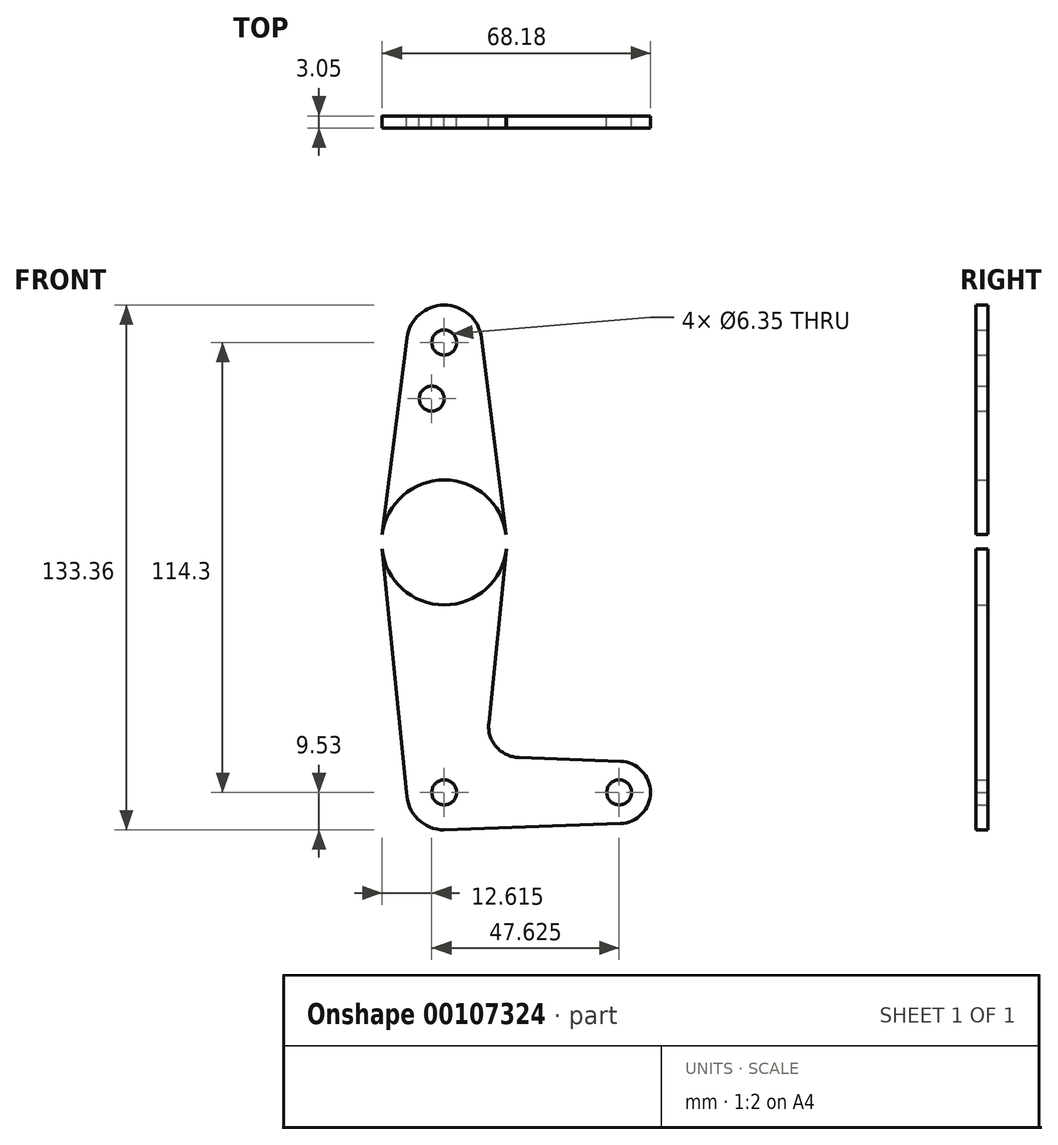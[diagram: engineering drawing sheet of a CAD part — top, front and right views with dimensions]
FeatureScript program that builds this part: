
annotation { "Feature Type Name" : "Feature", "Feature Type Description" : "" }
export const myFeature = defineFeature(function(context is Context, id is Id, definition is map)
    precondition{}
    {
        {
            var Q0;
            Q0=qCreatedBy(makeId("Front.planeOp"),FACE);
            var sketch = newSketch(context, id + "F0", { "sketchPlane" : qUnion([Q0])});
            skLineSegment(sketch, "E0", {"start": v(0, 114.3) * mm, "end": v(0, 0) * mm});
            skLineSegment(sketch, "E1", {"start": v(0, 0) * mm, "end": v(44.45, 0) * mm});
            skCircle(sketch, "E2", {"center": v(0, 114.3) * mm, "radius": 9.53 * mm});
            skCircle(sketch, "E3", {"center": v(0, 63.5) * mm, "radius": 15.88 * mm});
            skCircle(sketch, "E4", {"center": v(0, 0) * mm, "radius": 9.53 * mm});
            skCircle(sketch, "E5", {"center": v(44.45, 0) * mm, "radius": 7.94 * mm});
            skLineSegment(sketch, "E6", {"start": v(-9.45, 115.5) * mm, "end": v(-15.75, 65.48) * mm});
            skLineSegment(sketch, "E7", {"start": v(9.45, 115.5) * mm, "end": v(15.75, 65.48) * mm});
            skLineSegment(sketch, "E8", {"start": v(-9.52, 0) * mm, "end": v(-15.8, 61.9) * mm});
            skLineSegment(sketch, "E9", {"start": v(11.3, 17.6) * mm, "end": v(15.8, 61.9) * mm});
            skLineSegment(sketch, "E10", {"start": v(18.93, 8.85) * mm, "end": v(44.73, 7.93) * mm});
            skLineSegment(sketch, "E11", {"start": v(0, -9.53) * mm, "end": v(44.73, -7.93) * mm});
            skCircle(sketch, "E12", {"center": v(0, 114.3) * mm, "radius": 3.18 * mm});
            skCircle(sketch, "E13", {"center": v(-3.17, 100.03) * mm, "radius": 3.18 * mm});
            skCircle(sketch, "E14", {"center": v(0, 63.5) * mm, "radius": 3.18 * mm});
            skCircle(sketch, "E15", {"center": v(0, 0) * mm, "radius": 3.18 * mm});
            skCircle(sketch, "E16", {"center": v(44.45, 0) * mm, "radius": 3.18 * mm});
            skArc(sketch, "E17.filletArc", {"start": v(11.3, 17.6) * mm, "mid": v(13.22, 11.57) * mm, "end": v(18.93, 8.85) * mm});
            skSolve(sketch);
        }
        {
            var Q0;
            {var subQ0=sQuery(id+"F0.wireOp",EDGE,"E7");Q0=makeQuery(id+"F0.imprint","IMPRINT",FACE,{"disambiguationData":[TD([[makeQuery(id+"F0.imprint","IMPRINT",EDGE,{"derivedFrom":subQ0}),-1.0]])]});}
            var Q1;
            {var subQ0=sQuery(id+"F0.wireOp",EDGE,"E6");Q1=makeQuery(id+"F0.imprint","IMPRINT",FACE,{"disambiguationData":[TD([[makeQuery(id+"F0.imprint","IMPRINT",EDGE,{"derivedFrom":subQ0}),1.0]])]});}
            var Q2;
            Q2=makeQuery(id+"F0.imprint","IMPRINT",FACE,{"disambiguationData":[TD([[makeQuery(id+"F0.imprint","IMPRINT",EDGE,{"derivedFrom":sQuery(id+"F0.wireOp",EDGE,"E12")}),-1.0]])]});
            var Q3;
            {var subQ0=sQuery(id+"F0.wireOp",EDGE,"E3");var subQ2=sQuery(id+"F0.wireOp",EDGE,"E0");var subQ3=makeQuery(id+"F0.imprint","INTERSECT",VERTEX,{"disambiguationData":[OD(0.0)],"derivedFrom":[subQ2,subQ0]});Q3=makeQuery(id+"F0.imprint","IMPRINT",FACE,{"disambiguationData":[TD([[makeQuery(id+"F0.imprint","IMPRINT",EDGE,{"disambiguationData":[TD([[subQ3,-1.0]])],"derivedFrom":subQ2}),1.0]])]});}
            var Q4;
            {var subQ0=sQuery(id+"F0.wireOp",EDGE,"E9");Q4=makeQuery(id+"F0.imprint","IMPRINT",FACE,{"disambiguationData":[TD([[makeQuery(id+"F0.imprint","IMPRINT",EDGE,{"derivedFrom":subQ0}),1.0]])]});}
            var Q5;
            {var subQ5=sQuery(id+"F0.wireOp",EDGE,"E8");Q5=makeQuery(id+"F0.imprint","IMPRINT",FACE,{"disambiguationData":[TD([[makeQuery(id+"F0.imprint","IMPRINT",EDGE,{"derivedFrom":subQ5}),-1.0]])]});}
            var Q6;
            {var subQ0=sQuery(id+"F0.wireOp",EDGE,"E3");var subQ2=sQuery(id+"F0.wireOp",EDGE,"E0");var subQ3=makeQuery(id+"F0.imprint","INTERSECT",VERTEX,{"disambiguationData":[OD(0.0)],"derivedFrom":[subQ2,subQ0]});Q6=makeQuery(id+"F0.imprint","IMPRINT",FACE,{"disambiguationData":[TD([[makeQuery(id+"F0.imprint","IMPRINT",EDGE,{"disambiguationData":[TD([[subQ3,-1.0]])],"derivedFrom":subQ2}),-1.0]])]});}
            var Q7;
            {var subQ0=sQuery(id+"F0.wireOp",EDGE,"E4");var subQ1=sQuery(id+"F0.wireOp",EDGE,"E0");var subQ2=makeQuery(id+"F0.imprint","INTERSECT",VERTEX,{"derivedFrom":[subQ1,subQ0]});Q7=makeQuery(id+"F0.imprint","IMPRINT",FACE,{"disambiguationData":[TD([[makeQuery(id+"F0.imprint","IMPRINT",EDGE,{"disambiguationData":[TD([[subQ2,-1.0]])],"derivedFrom":subQ1}),1.0]])]});}
            var Q8;
            {var subQ3=sQuery(id+"F0.wireOp",EDGE,"E4");var subQ9=sQuery(id+"F0.wireOp",EDGE,"E0");var subQ11=makeQuery(id+"F0.imprint","INTERSECT",VERTEX,{"derivedFrom":[subQ9,subQ3]});Q8=makeQuery(id+"F0.imprint","IMPRINT",FACE,{"disambiguationData":[TD([[makeQuery(id+"F0.imprint","IMPRINT",EDGE,{"disambiguationData":[TD([[subQ11,-1.0]])],"derivedFrom":subQ9}),-1.0]])]});}
            var Q9;
            Q9=makeQuery(id+"F0.imprint","IMPRINT",FACE,{"disambiguationData":[TD([[makeQuery(id+"F0.imprint","IMPRINT",EDGE,{"derivedFrom":sQuery(id+"F0.wireOp",EDGE,"E16")}),-1.0]])]});
            var Q10;
            {var subQ0=sQuery(id+"F0.wireOp",EDGE,"E5");var subQ1=sQuery(id+"F0.wireOp",EDGE,"E1");var subQ2=makeQuery(id+"F0.imprint","INTERSECT",VERTEX,{"derivedFrom":[subQ1,subQ0]});Q10=makeQuery(id+"F0.imprint","IMPRINT",FACE,{"disambiguationData":[TD([[makeQuery(id+"F0.imprint","IMPRINT",EDGE,{"disambiguationData":[TD([[subQ2,1.0]])],"derivedFrom":subQ1}),-1.0]])]});}
            extrude(context, id + "F1", {"entities" : qUnion([Q0, Q1, Q2, Q3, Q4, Q5, Q6, Q7, Q8, Q9, Q10]), "depth" : 3.05 * mm});
        }
    });
